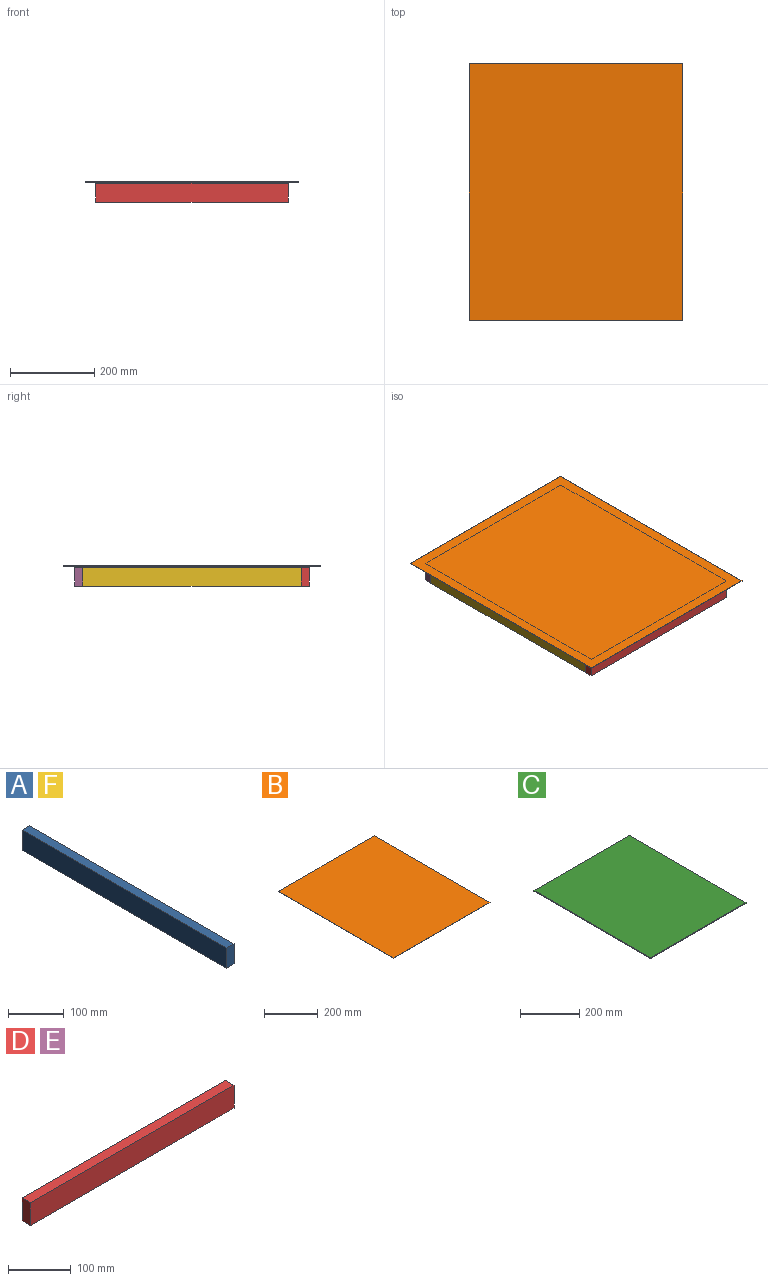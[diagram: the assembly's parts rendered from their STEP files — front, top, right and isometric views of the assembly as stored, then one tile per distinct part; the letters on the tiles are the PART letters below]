
ASSEMBLY  parts=6 mates=5
PART A: 6 faces, bbox 19.1x520.7x44.5 mm
  f0: plane 520.7x44.45mm, normal (-1,0,0), area 23145.1mm2, adj f1,f3,f4,f5
  f1: plane 520.7x19.05mm, normal (0,0,-1), area 9919.3mm2, adj f0,f2,f4,f5
  f2: plane 520.7x44.45mm, normal (1,0,0), area 23145.1mm2, adj f1,f3,f4,f5
  f3: plane 520.7x19.05mm, normal (0,0,1), area 9919.3mm2, adj f0,f2,f4,f5
  f4: plane 44.45x19.05mm, normal (0,-1,0), area 846.8mm2, adj f0,f1,f2,f3
  f5: plane 44.45x19.05mm, normal (0,1,0), area 846.8mm2, adj f0,f1,f2,f3
PART B: 6 faces, bbox 508x609.6x0.8 mm
  f0: plane 609.6x508mm, normal (0,0,-1), area 309676.8mm2, adj f1,f3,f4,f5
  f1: plane 609.6x0.79mm, normal (1,0,0), area 483.9mm2, adj f0,f2,f4,f5
  f2: plane 609.6x508mm, normal (0,0,1), area 309676.8mm2, adj f1,f3,f4,f5
  f3: plane 609.6x0.79mm, normal (-1,0,0), area 483.9mm2, adj f0,f2,f4,f5
  f4: plane 508x0.79mm, normal (0,-1,0), area 403.2mm2, adj f0,f1,f2,f3
  f5: plane 508x0.79mm, normal (0,1,0), area 403.2mm2, adj f0,f1,f2,f3
PART C: 6 faces, bbox 457.2x558.8x3.2 mm
  f0: plane 558.8x3.18mm, normal (-1,0,0), area 1774.2mm2, adj f1,f3,f4,f5
  f1: plane 558.8x457.2mm, normal (0,0,-1), area 255483.4mm2, adj f0,f2,f4,f5
  f2: plane 558.8x3.18mm, normal (1,0,0), area 1774.2mm2, adj f1,f3,f4,f5
  f3: plane 558.8x457.2mm, normal (0,0,1), area 255483.4mm2, adj f0,f2,f4,f5
  f4: plane 457.2x3.18mm, normal (0,-1,0), area 1451.6mm2, adj f0,f1,f2,f3
  f5: plane 457.2x3.18mm, normal (0,1,0), area 1451.6mm2, adj f0,f1,f2,f3
PART D: 6 faces, bbox 457.2x19.1x44.5 mm
  f0: plane 457.2x19.05mm, normal (0,0,1), area 8709.7mm2, adj f1,f3,f4,f5
  f1: plane 44.45x19.05mm, normal (-1,0,0), area 846.8mm2, adj f0,f2,f4,f5
  f2: plane 457.2x19.05mm, normal (0,0,-1), area 8709.7mm2, adj f1,f3,f4,f5
  f3: plane 44.45x19.05mm, normal (1,0,0), area 846.8mm2, adj f0,f2,f4,f5
  f4: plane 457.2x44.45mm, normal (0,-1,0), area 20322.5mm2, adj f0,f1,f2,f3
  f5: plane 457.2x44.45mm, normal (0,1,0), area 20322.5mm2, adj f0,f1,f2,f3
PART E: same geometry as D
PART F: same geometry as A
PLACE A rot(axis=(0,0,1),180deg) t=(-19.05,-539.75,0)mm
PLACE B t=(0,25.4,0)mm
PLACE C at identity
PLACE D rot(axis=(0,0,1),180deg) t=(0,-558.8,0)mm
PLACE E at identity
PLACE F t=(19.05,-19.05,0)mm
MATE fastened A.f0 <-> D.f1  axis (1,0,0) through (228.6,-539.75,0)mm
MATE fastened A.f0 <-> E.f3  axis (1,0,0) through (228.6,-19.05,0)mm
MATE fastened D.f5 <-> C.f4  axis (0,-1,0) through (0,-558.8,22.23)mm
MATE fastened C.f3 <-> B.f0  axis (0,0,1) through (0,-279.4,25.4)mm
MATE fastened F.f0 <-> E.f1  axis (-1,0,0) through (-228.6,-19.05,0)mm
